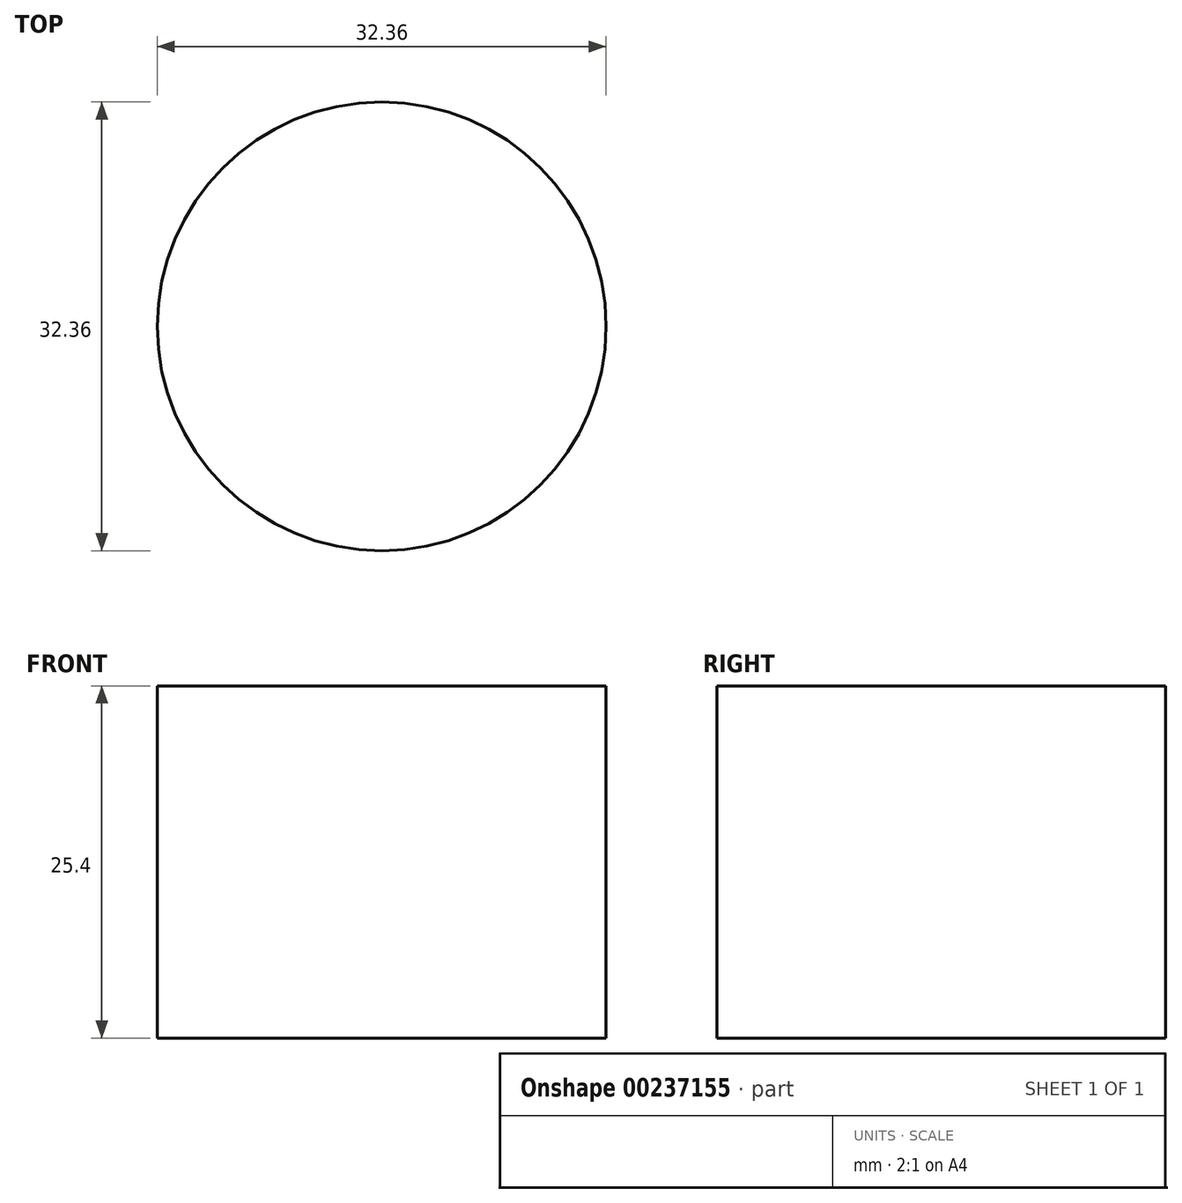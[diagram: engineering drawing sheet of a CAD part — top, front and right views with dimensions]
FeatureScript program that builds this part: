
annotation { "Feature Type Name" : "Feature", "Feature Type Description" : "" }
export const myFeature = defineFeature(function(context is Context, id is Id, definition is map)
    precondition{}
    {
        {
            var Q0;
            Q0=qCreatedBy(makeId("Top.planeOp"),FACE);
            var sketch = newSketch(context, id + "F0", { "sketchPlane" : qUnion([Q0])});
            skCircle(sketch, "E0", {"center": v(0, 0) * mm, "radius": 16.18 * mm});
            skSolve(sketch);
        }
        {
            var Q0;
            Q0=makeQuery(id+"F0.imprint","IMPRINT",FACE,{"disambiguationData":[TD([[makeQuery(id+"F0.imprint","IMPRINT",EDGE,{"derivedFrom":sQuery(id+"F0.wireOp",EDGE,"E0")}),1.0]])]});
            extrude(context, id + "F1", {"entities" : qUnion([Q0]), "depth" : 25.4 * mm});
        }
    });
